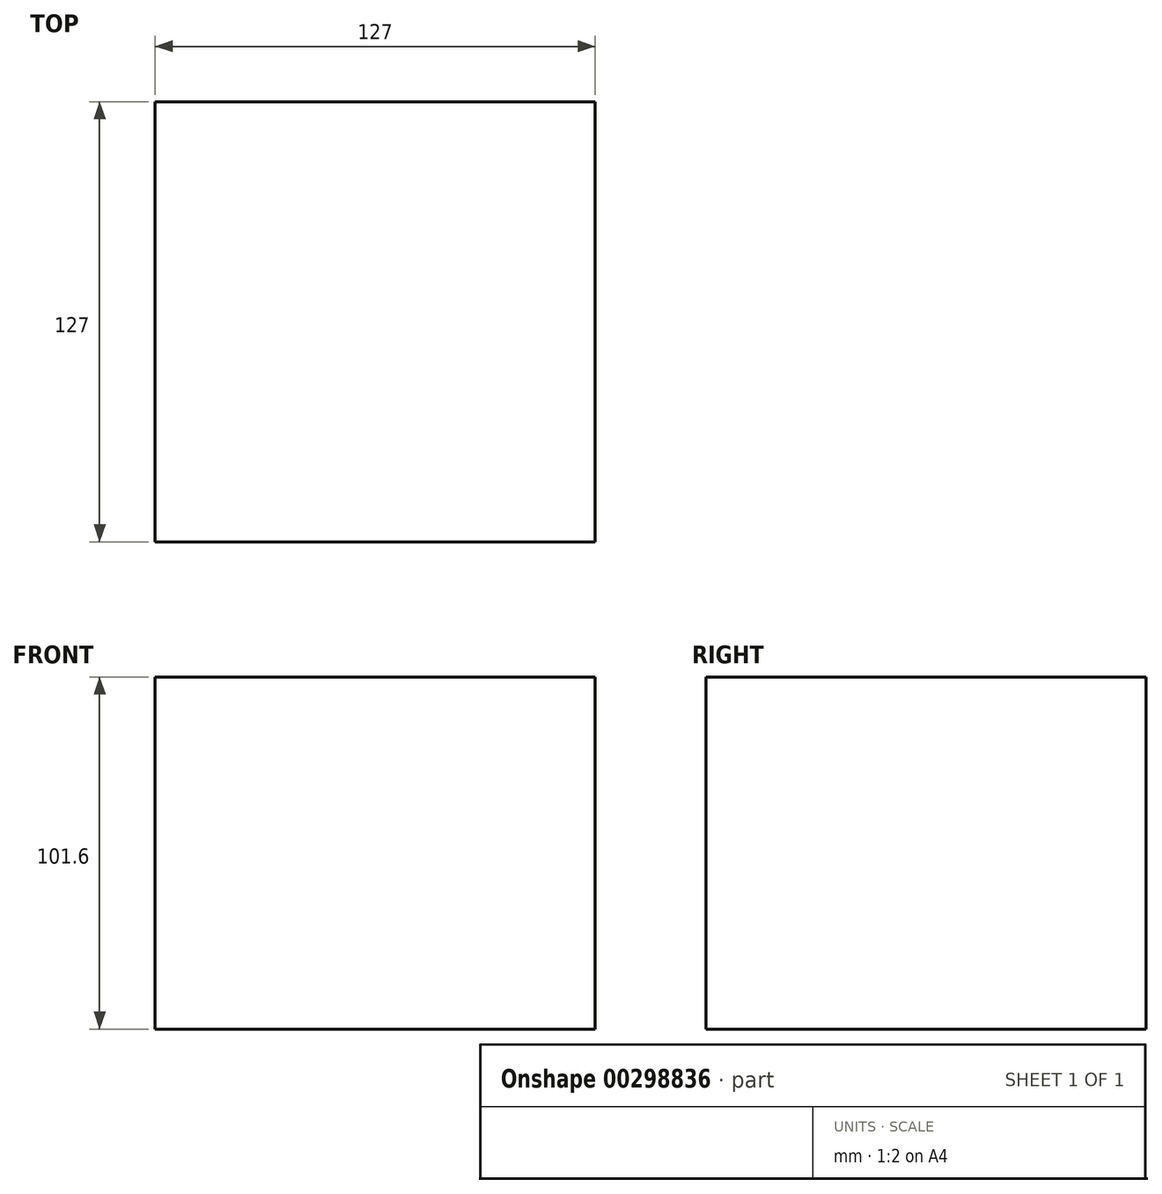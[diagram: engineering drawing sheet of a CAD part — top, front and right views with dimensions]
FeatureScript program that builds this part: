
annotation { "Feature Type Name" : "Feature", "Feature Type Description" : "" }
export const myFeature = defineFeature(function(context is Context, id is Id, definition is map)
    precondition{}
    {
        {
            var Q0;
            Q0=qCreatedBy(makeId("Top.planeOp"),FACE);
            var sketch = newSketch(context, id + "F0", { "sketchPlane" : qUnion([Q0])});
            skLineSegment(sketch, "E0.bottom", {"start": v(-60.2, 76.82) * mm, "end": v(66.8, 76.82) * mm});
            skLineSegment(sketch, "E0.top", {"start": v(-60.2, -50.18) * mm, "end": v(66.8, -50.18) * mm});
            skLineSegment(sketch, "E0.left", {"start": v(-60.2, 76.82) * mm, "end": v(-60.2, -50.18) * mm});
            skLineSegment(sketch, "E0.right", {"start": v(66.8, 76.82) * mm, "end": v(66.8, -50.18) * mm});
            skSolve(sketch);
        }
        {
            var Q0;
            Q0=makeQuery(id+"F0.imprint","IMPRINT",FACE,{"disambiguationData":[TD([[makeQuery(id+"F0.imprint","IMPRINT",EDGE,{"derivedFrom":sQuery(id+"F0.wireOp",EDGE,"E0.bottom")}),-1.0]])]});
            extrude(context, id + "F1", {"entities" : qUnion([Q0]), "depth" : 101.6 * mm});
        }
    });
